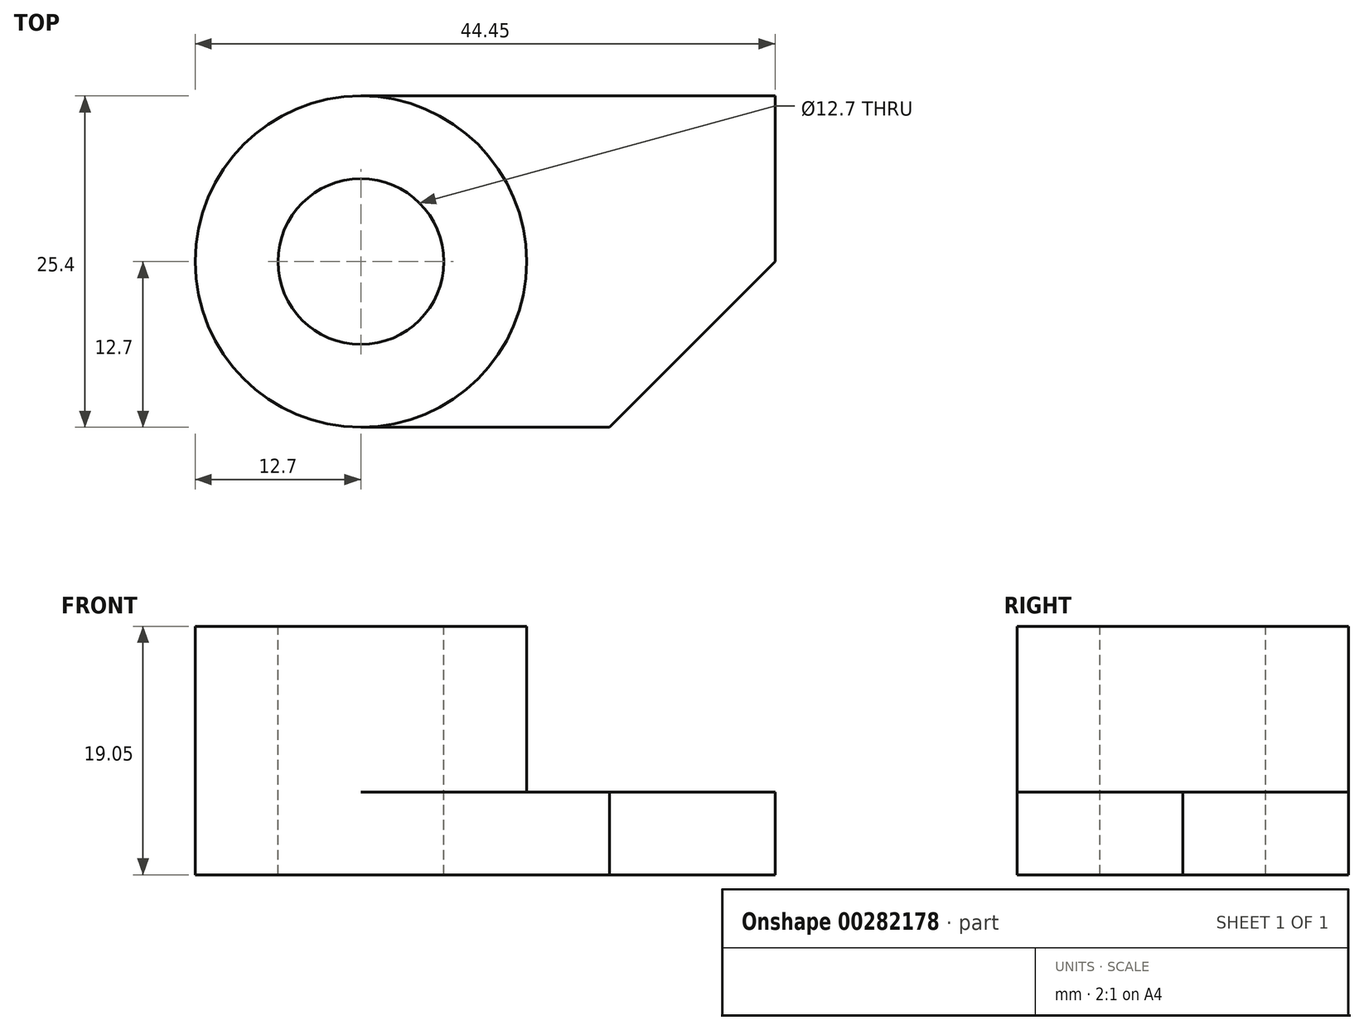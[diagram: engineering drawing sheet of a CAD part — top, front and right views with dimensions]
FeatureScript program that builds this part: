
annotation { "Feature Type Name" : "Feature", "Feature Type Description" : "" }
export const myFeature = defineFeature(function(context is Context, id is Id, definition is map)
    precondition{}
    {
        {
            var Q0;
            Q0=qCreatedBy(makeId("Top.planeOp"),FACE);
            var sketch = newSketch(context, id + "F0", { "sketchPlane" : qUnion([Q0])});
            skCircle(sketch, "E0", {"center": v(0, 0) * mm, "radius": 6.35 * mm});
            skCircle(sketch, "E1", {"center": v(0, 0) * mm, "radius": 12.7 * mm});
            skSolve(sketch);
        }
        {
            var Q0;
            Q0=makeQuery(id+"F0.imprint","IMPRINT",FACE,{"disambiguationData":[TD([[makeQuery(id+"F0.imprint","IMPRINT",EDGE,{"derivedFrom":sQuery(id+"F0.wireOp",EDGE,"E0")}),-1.0]])]});
            extrude(context, id + "F1", {"entities" : qUnion([Q0]), "oppositeDirection" : true, "depth" : 12.7 * mm});
        }
        {
            var Q0;
            Q0=makeQuery(id+"F1.opExtrude","CAP_FACE",FACE,{"disambiguationData":[OSD([sQuery(id+"F0.wireOp",EDGE,"E0"),sQuery(id+"F0.wireOp",EDGE,"E1")])],"isStart":false});
            var sketch = newSketch(context, id + "F2", { "sketchPlane" : qUnion([Q0])});
            skLineSegment(sketch, "E2", {"start": v(0, 12.7) * mm, "end": v(19.05, 12.7) * mm});
            skLineSegment(sketch, "E3", {"start": v(0, -12.7) * mm, "end": v(31.75, -12.7) * mm});
            skLineSegment(sketch, "E4", {"start": v(31.75, -12.7) * mm, "end": v(31.75, 0) * mm});
            skLineSegment(sketch, "E5", {"start": v(31.75, 0) * mm, "end": v(19.05, 12.7) * mm});
            skSolve(sketch);
        }
        {
            var Q0;
            Q0=makeQuery(id+"F2.imprint","IMPRINT",FACE,{"disambiguationData":[TD([[makeQuery(id+"F2.imprint","IMPRINT",EDGE,{"derivedFrom":makeQuery(id+"F1.opExtrude","CAP_EDGE",EDGE,{"disambiguationData":[OSD([sQuery(id+"F0.wireOp",EDGE,"E0")])],"isStart":false})}),1.0]])]});
            var Q1;
            {var subQ1=sQuery(id+"F2.wireOp",EDGE,"E2");Q1=makeQuery(id+"F2.imprint","IMPRINT",FACE,{"disambiguationData":[TD([[makeQuery(id+"F2.imprint","IMPRINT",EDGE,{"derivedFrom":subQ1}),-1.0]])]});}
            extrude(context, id + "F3", {"entities" : qUnion([Q0, Q1]), "operationType" : NewBodyOperationType.ADD, "depth" : 6.35 * mm});
        }
    });
